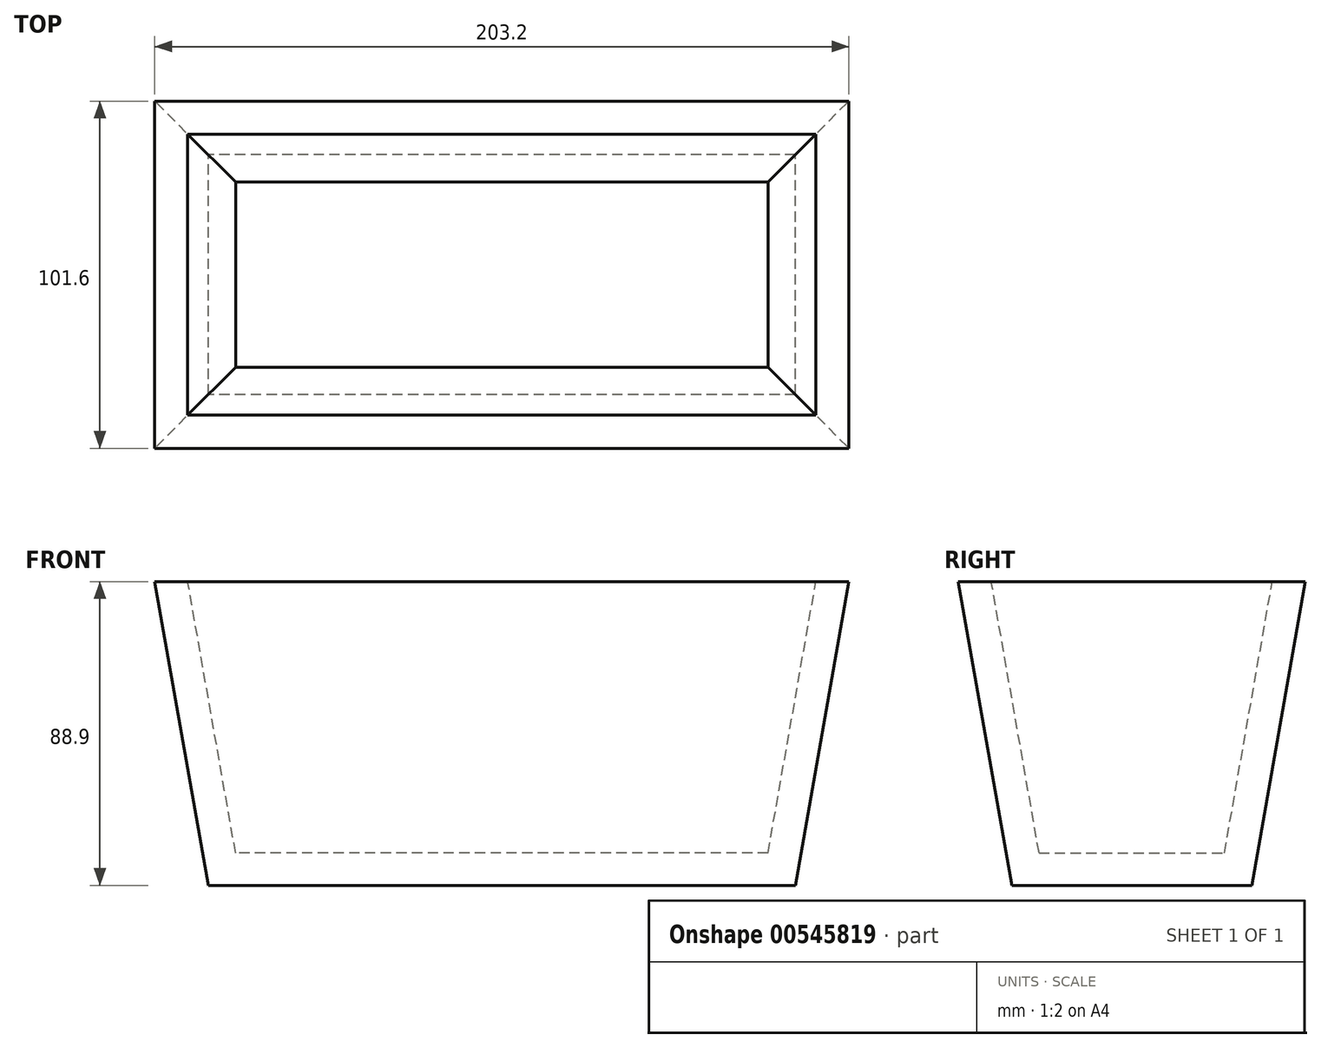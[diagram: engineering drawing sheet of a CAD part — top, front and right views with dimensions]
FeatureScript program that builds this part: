
annotation { "Feature Type Name" : "Feature", "Feature Type Description" : "" }
export const myFeature = defineFeature(function(context is Context, id is Id, definition is map)
    precondition{}
    {
        {
            var Q0;
            Q0=qCreatedBy(makeId("Front.planeOp"),FACE);
            var sketch = newSketch(context, id + "F0", { "sketchPlane" : qUnion([Q0])});
            skLineSegment(sketch, "E0", {"start": v(0, 0) * mm, "end": v(0, 88.9) * mm});
            skLineSegment(sketch, "E1", {"start": v(0, 88.9) * mm, "end": v(101.6, 88.9) * mm});
            skLineSegment(sketch, "E2", {"start": v(101.6, 88.9) * mm, "end": v(85.92, 0) * mm});
            skLineSegment(sketch, "E3", {"start": v(85.92, 0) * mm, "end": v(0, 0) * mm});
            skSolve(sketch);
        }
        {
            var Q0;
            Q0=makeQuery(id+"F0.imprint","IMPRINT",FACE,{"disambiguationData":[TD([[makeQuery(id+"F0.imprint","IMPRINT",EDGE,{"derivedFrom":sQuery(id+"F0.wireOp",EDGE,"E0")}),-1.0]])]});
            extrude(context, id + "F1", {"entities" : qUnion([Q0]), "depth" : 50.8 * mm, "offsetDistance" : 25.4 * mm});
        }
        {
            var Q0;
            Q0=qCreatedBy(makeId("Right.planeOp"),FACE);
            var sketch = newSketch(context, id + "F2", { "sketchPlane" : qUnion([Q0])});
            skLineSegment(sketch, "E4", {"start": v(-50.8, 88.9) * mm, "end": v(-35.12, 0) * mm});
            skLineSegment(sketch, "E5", {"start": v(-35.12, 0) * mm, "end": v(-50.8, 0) * mm});
            skLineSegment(sketch, "E6", {"start": v(-50.8, 0) * mm, "end": v(-50.8, 88.9) * mm});
            skSolve(sketch);
        }
        {
            var Q0;
            Q0=makeQuery(id+"F2.imprint","IMPRINT",FACE,{"disambiguationData":[TD([[makeQuery(id+"F2.imprint","IMPRINT",EDGE,{"derivedFrom":sQuery(id+"F2.wireOp",EDGE,"E4")}),-1.0]])]});
            extrude(context, id + "F3", {"entities" : qUnion([Q0]), "operationType" : NewBodyOperationType.REMOVE, "endBound" : BoundingType.THROUGH_ALL, "depth" : 25.4 * mm, "offsetDistance" : 25.4 * mm});
        }
        {
            var Q0;
            Q0=makeQuery(id+"F1.opExtrude","SWEPT_BODY",BODY,{"disambiguationData":[OSD([sQuery(id+"F0.wireOp",EDGE,"E0"),sQuery(id+"F0.wireOp",EDGE,"E1"),sQuery(id+"F0.wireOp",EDGE,"E2"),sQuery(id+"F0.wireOp",EDGE,"E3")])]});
            var Q1;
            Q1=qCreatedBy(makeId("Front.planeOp"),FACE);
            mirror(context, id + "F4", {"operationType" : NewBodyOperationType.ADD, "entities" : qUnion([Q0]), "mirrorPlane" : qUnion([Q1])});
        }
        {
            var Q0;
            Q0=makeQuery(id+"F1.opExtrude","SWEPT_BODY",BODY,{"disambiguationData":[OSD([sQuery(id+"F0.wireOp",EDGE,"E0"),sQuery(id+"F0.wireOp",EDGE,"E1"),sQuery(id+"F0.wireOp",EDGE,"E2"),sQuery(id+"F0.wireOp",EDGE,"E3")])]});
            var Q1;
            Q1=qCreatedBy(makeId("Right.planeOp"),FACE);
            mirror(context, id + "F5", {"operationType" : NewBodyOperationType.ADD, "entities" : qUnion([Q0]), "mirrorPlane" : qUnion([Q1])});
        }
        {
            var Q0;
            {var subQ0=makeQuery(id+"F1.opExtrude","SWEPT_FACE",FACE,{"disambiguationData":[OSD([sQuery(id+"F0.wireOp",EDGE,"E1")])]});var subQ1=makeQuery(id+"F4.boolean.opBoolean","MERGE",FACE,{"derivedFrom":[subQ0,makeQuery(id+"F4.opPattern","COPY",FACE,{"derivedFrom":subQ0,"instanceName":"1"})]});Q0=makeQuery(id+"F5.boolean.opBoolean","MERGE",FACE,{"derivedFrom":[subQ1,makeQuery(id+"F5.opPattern","COPY",FACE,{"derivedFrom":subQ1,"instanceName":"1"})]});}
            shell(context, id + "F6", {"entities" : qUnion([Q0]), "thickness" : 9.52 * mm});
        }
    });
